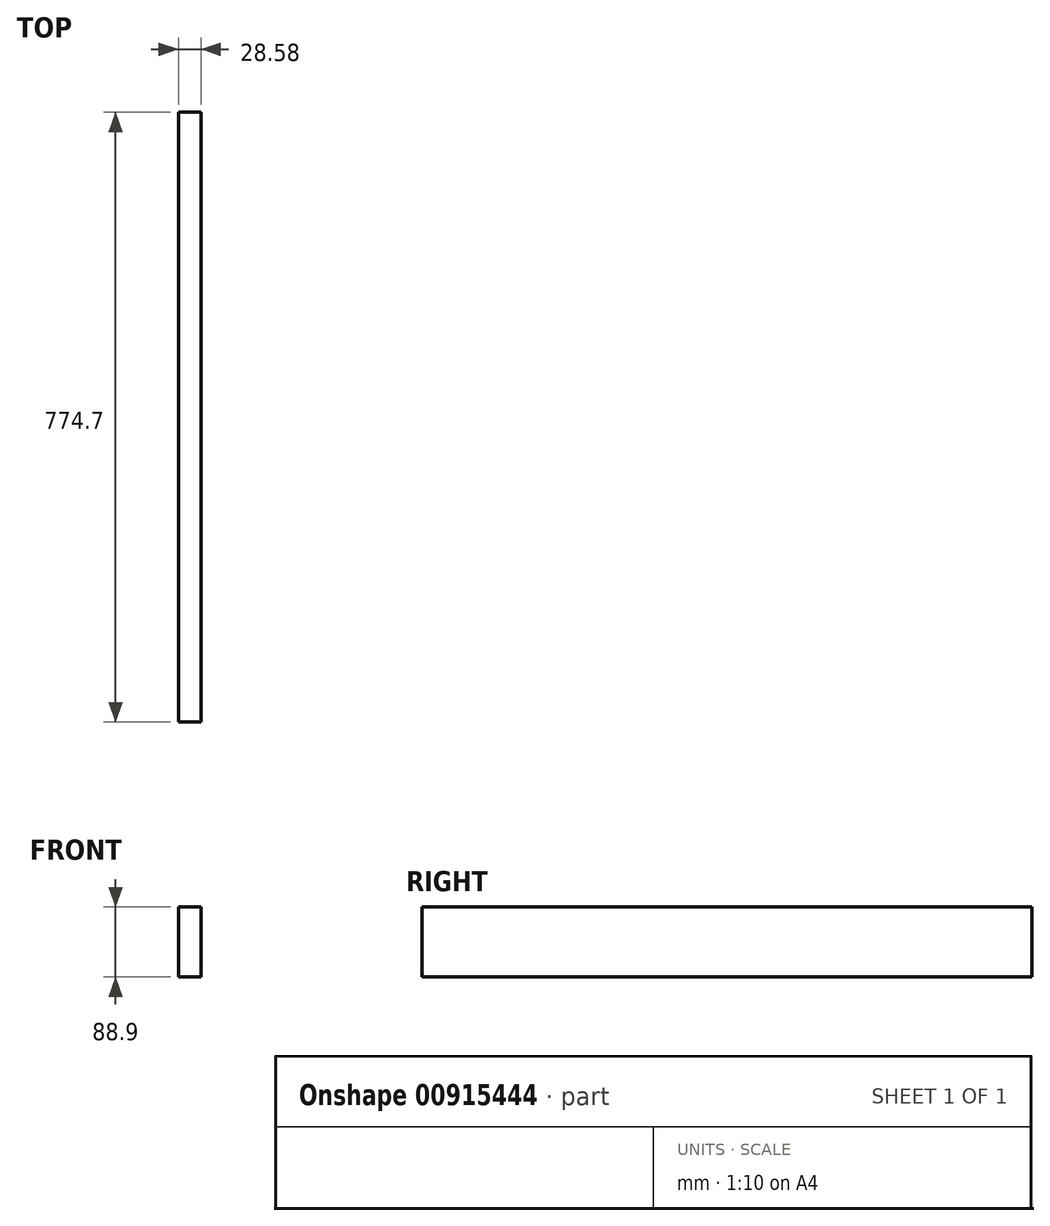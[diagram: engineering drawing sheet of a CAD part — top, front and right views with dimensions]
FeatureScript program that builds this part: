
annotation { "Feature Type Name" : "Feature", "Feature Type Description" : "" }
export const myFeature = defineFeature(function(context is Context, id is Id, definition is map)
    precondition{}
    {
        {
            var Q0;
            Q0=qCreatedBy(makeId("Front.planeOp"),FACE);
            var sketch = newSketch(context, id + "F0", { "sketchPlane" : qUnion([Q0])});
            skLineSegment(sketch, "E0.bottom", {"start": v(14.29, 44.45) * mm, "end": v(-14.29, 44.45) * mm});
            skLineSegment(sketch, "E0.top", {"start": v(14.29, -44.45) * mm, "end": v(-14.29, -44.45) * mm});
            skLineSegment(sketch, "E0.left", {"start": v(14.29, 44.45) * mm, "end": v(14.29, -44.45) * mm});
            skLineSegment(sketch, "E0.right", {"start": v(-14.29, 44.45) * mm, "end": v(-14.29, -44.45) * mm});
            skPoint(sketch, "E0.middle", {"position": v(0, 0) * mm});
            skSolve(sketch);
        }
        {
            var Q0;
            Q0=makeQuery(id+"F0.imprint","IMPRINT",FACE,{"disambiguationData":[TD([[makeQuery(id+"F0.imprint","IMPRINT",EDGE,{"derivedFrom":sQuery(id+"F0.wireOp",EDGE,"E0.bottom")}),1.0]])]});
            extrude(context, id + "F1", {"entities" : qUnion([Q0]), "depth" : 387.35 * mm, "offsetDistance" : 25.4 * mm, "hasSecondDirection" : true, "secondDirectionOppositeDirection" : true, "secondDirectionDepth" : 387.35 * mm});
        }
    });
